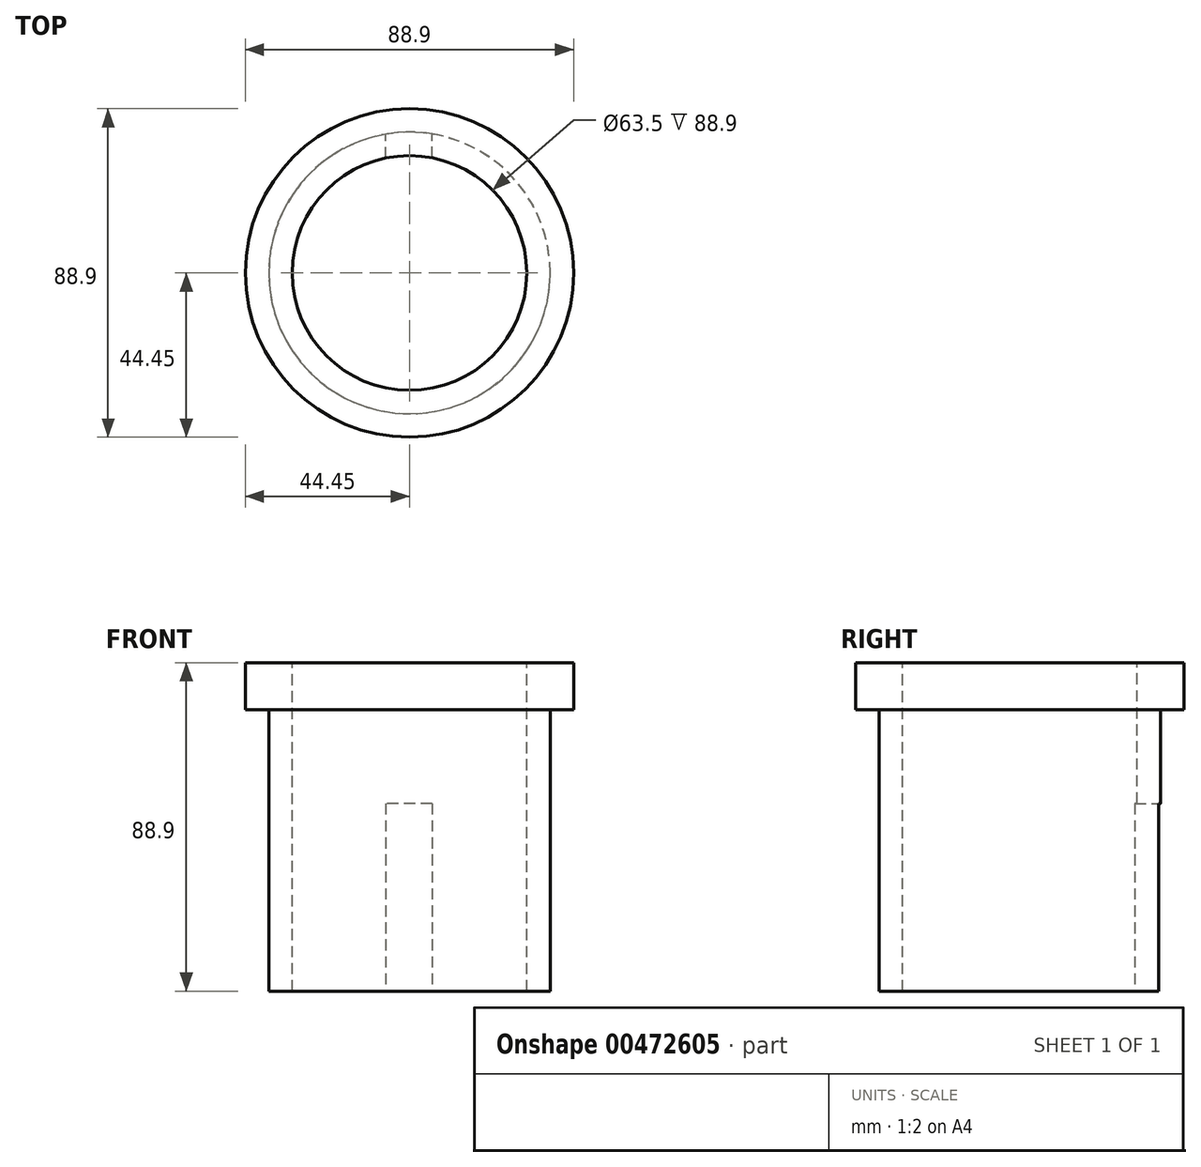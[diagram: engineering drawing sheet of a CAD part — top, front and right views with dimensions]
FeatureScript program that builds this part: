
annotation { "Feature Type Name" : "Feature", "Feature Type Description" : "" }
export const myFeature = defineFeature(function(context is Context, id is Id, definition is map)
    precondition{}
    {
        {
            var Q0;
            Q0=qCreatedBy(makeId("Top.planeOp"),FACE);
            var sketch = newSketch(context, id + "F0", { "sketchPlane" : qUnion([Q0])});
            skSolve(sketch);
        }
        {
            var Q0;
            Q0=qCreatedBy(makeId("Top.planeOp"),FACE);
            var sketch = newSketch(context, id + "F1", { "sketchPlane" : qUnion([Q0])});
            skCircle(sketch, "E0", {"center": v(0, 0) * mm, "radius": 44.45 * mm});
            skCircle(sketch, "E1", {"center": v(0, 0) * mm, "radius": 38.1 * mm});
            skCircle(sketch, "E2", {"center": v(0, 0) * mm, "radius": 31.75 * mm});
            skLineSegment(sketch, "E3.left", {"start": v(-6.35, 37.57) * mm, "end": v(-6.35, -37.57) * mm});
            skLineSegment(sketch, "E3.right", {"start": v(6.35, 37.57) * mm, "end": v(6.35, -37.57) * mm});
            skSolve(sketch);
        }
        {
            var Q0;
            {var subQ0=sQuery(id+"F1.wireOp",EDGE,"E3.left");var subQ1=sQuery(id+"F1.wireOp",EDGE,"E1");var subQ2=makeQuery(id+"F1.imprint","INTERSECT",VERTEX,{"disambiguationData":[OD(0.0)],"derivedFrom":[subQ1,subQ0]});Q0=makeQuery(id+"F1.imprint","IMPRINT",FACE,{"disambiguationData":[TD([[makeQuery(id+"F1.imprint","IMPRINT",EDGE,{"disambiguationData":[TD([[subQ2,1.0]])],"derivedFrom":subQ1}),1.0]])]});}
            var Q1;
            {var subQ0=sQuery(id+"F1.wireOp",EDGE,"E3.left");var subQ1=sQuery(id+"F1.wireOp",EDGE,"E1");var subQ2=makeQuery(id+"F1.imprint","INTERSECT",VERTEX,{"disambiguationData":[OD(0.0)],"derivedFrom":[subQ1,subQ0]});Q1=makeQuery(id+"F1.imprint","IMPRINT",FACE,{"disambiguationData":[TD([[makeQuery(id+"F1.imprint","IMPRINT",EDGE,{"disambiguationData":[TD([[subQ2,-1.0]])],"derivedFrom":subQ1}),1.0]])]});}
            var Q2;
            {var subQ0=sQuery(id+"F1.wireOp",EDGE,"E3.right");var subQ1=sQuery(id+"F1.wireOp",EDGE,"E1");var subQ2=makeQuery(id+"F1.imprint","INTERSECT",VERTEX,{"disambiguationData":[OD(0.0)],"derivedFrom":[subQ1,subQ0]});Q2=makeQuery(id+"F1.imprint","IMPRINT",FACE,{"disambiguationData":[TD([[makeQuery(id+"F1.imprint","IMPRINT",EDGE,{"disambiguationData":[TD([[subQ2,1.0]])],"derivedFrom":subQ1}),1.0]])]});}
            var Q3;
            {var subQ0=sQuery(id+"F1.wireOp",EDGE,"E3.left");var subQ1=sQuery(id+"F1.wireOp",EDGE,"E1");var subQ2=makeQuery(id+"F1.imprint","INTERSECT",VERTEX,{"disambiguationData":[OD(1.0)],"derivedFrom":[subQ1,subQ0]});Q3=makeQuery(id+"F1.imprint","IMPRINT",FACE,{"disambiguationData":[TD([[makeQuery(id+"F1.imprint","IMPRINT",EDGE,{"disambiguationData":[TD([[subQ2,-1.0]])],"derivedFrom":subQ1}),1.0]])]});}
            extrude(context, id + "F2", {"entities" : qUnion([Q0, Q1, Q2, Q3]), "oppositeDirection" : true, "depth" : 76.2 * mm});
        }
        {
            var Q0;
            Q0 = qSketchRegion(id + "F0", true);
            var Q1;
            Q1=makeQuery(id+"F1.imprint","IMPRINT",FACE,{"disambiguationData":[TD([[makeQuery(id+"F1.imprint","IMPRINT",EDGE,{"derivedFrom":sQuery(id+"F1.wireOp",EDGE,"E0")}),1.0]])]});
            var Q2;
            {var subQ0=sQuery(id+"F1.wireOp",EDGE,"E3.left");var subQ1=sQuery(id+"F1.wireOp",EDGE,"E1");var subQ2=makeQuery(id+"F1.imprint","INTERSECT",VERTEX,{"disambiguationData":[OD(0.0)],"derivedFrom":[subQ1,subQ0]});Q2=makeQuery(id+"F1.imprint","IMPRINT",FACE,{"disambiguationData":[TD([[makeQuery(id+"F1.imprint","IMPRINT",EDGE,{"disambiguationData":[TD([[subQ2,-1.0]])],"derivedFrom":subQ1}),1.0]])]});}
            var Q3;
            {var subQ0=sQuery(id+"F1.wireOp",EDGE,"E3.right");var subQ1=sQuery(id+"F1.wireOp",EDGE,"E1");var subQ2=makeQuery(id+"F1.imprint","INTERSECT",VERTEX,{"disambiguationData":[OD(0.0)],"derivedFrom":[subQ1,subQ0]});Q3=makeQuery(id+"F1.imprint","IMPRINT",FACE,{"disambiguationData":[TD([[makeQuery(id+"F1.imprint","IMPRINT",EDGE,{"disambiguationData":[TD([[subQ2,1.0]])],"derivedFrom":subQ1}),1.0]])]});}
            var Q4;
            {var subQ0=sQuery(id+"F1.wireOp",EDGE,"E3.left");var subQ1=sQuery(id+"F1.wireOp",EDGE,"E1");var subQ2=makeQuery(id+"F1.imprint","INTERSECT",VERTEX,{"disambiguationData":[OD(1.0)],"derivedFrom":[subQ1,subQ0]});Q4=makeQuery(id+"F1.imprint","IMPRINT",FACE,{"disambiguationData":[TD([[makeQuery(id+"F1.imprint","IMPRINT",EDGE,{"disambiguationData":[TD([[subQ2,-1.0]])],"derivedFrom":subQ1}),1.0]])]});}
            var Q5;
            {var subQ0=sQuery(id+"F1.wireOp",EDGE,"E3.left");var subQ1=sQuery(id+"F1.wireOp",EDGE,"E1");var subQ2=makeQuery(id+"F1.imprint","INTERSECT",VERTEX,{"disambiguationData":[OD(0.0)],"derivedFrom":[subQ1,subQ0]});Q5=makeQuery(id+"F1.imprint","IMPRINT",FACE,{"disambiguationData":[TD([[makeQuery(id+"F1.imprint","IMPRINT",EDGE,{"disambiguationData":[TD([[subQ2,1.0]])],"derivedFrom":subQ1}),1.0]])]});}
            extrude(context, id + "F3", {"entities" : qUnion([Q0, Q1, Q2, Q3, Q4, Q5]), "operationType" : NewBodyOperationType.ADD, "depth" : 12.7 * mm});
        }
        {
            var Q0;
            Q0=makeQuery(id+"F2.opExtrude","CAP_FACE",FACE,{"disambiguationData":[OSD([sQuery(id+"F1.wireOp",EDGE,"E1"),sQuery(id+"F1.wireOp",EDGE,"E2")])],"isStart":false});
            var sketch = newSketch(context, id + "F4", { "sketchPlane" : qUnion([Q0])});
            skLineSegment(sketch, "E4", {"start": v(-6.46, -31.09) * mm, "end": v(-6.46, -37.55) * mm});
            skLineSegment(sketch, "E5", {"start": v(6.13, -31.15) * mm, "end": v(6.13, -37.6) * mm});
            skSolve(sketch);
        }
        {
            var Q0;
            {var subQ0=sQuery(id+"F4.wireOp",EDGE,"E4");Q0=makeQuery(id+"F4.imprint","IMPRINT",FACE,{"disambiguationData":[TD([[makeQuery(id+"F4.imprint","IMPRINT",EDGE,{"derivedFrom":subQ0}),1.0]])]});}
            extrude(context, id + "F5", {"entities" : qUnion([Q0]), "operationType" : NewBodyOperationType.REMOVE, "oppositeDirection" : true, "depth" : 50.8 * mm});
        }
    });
